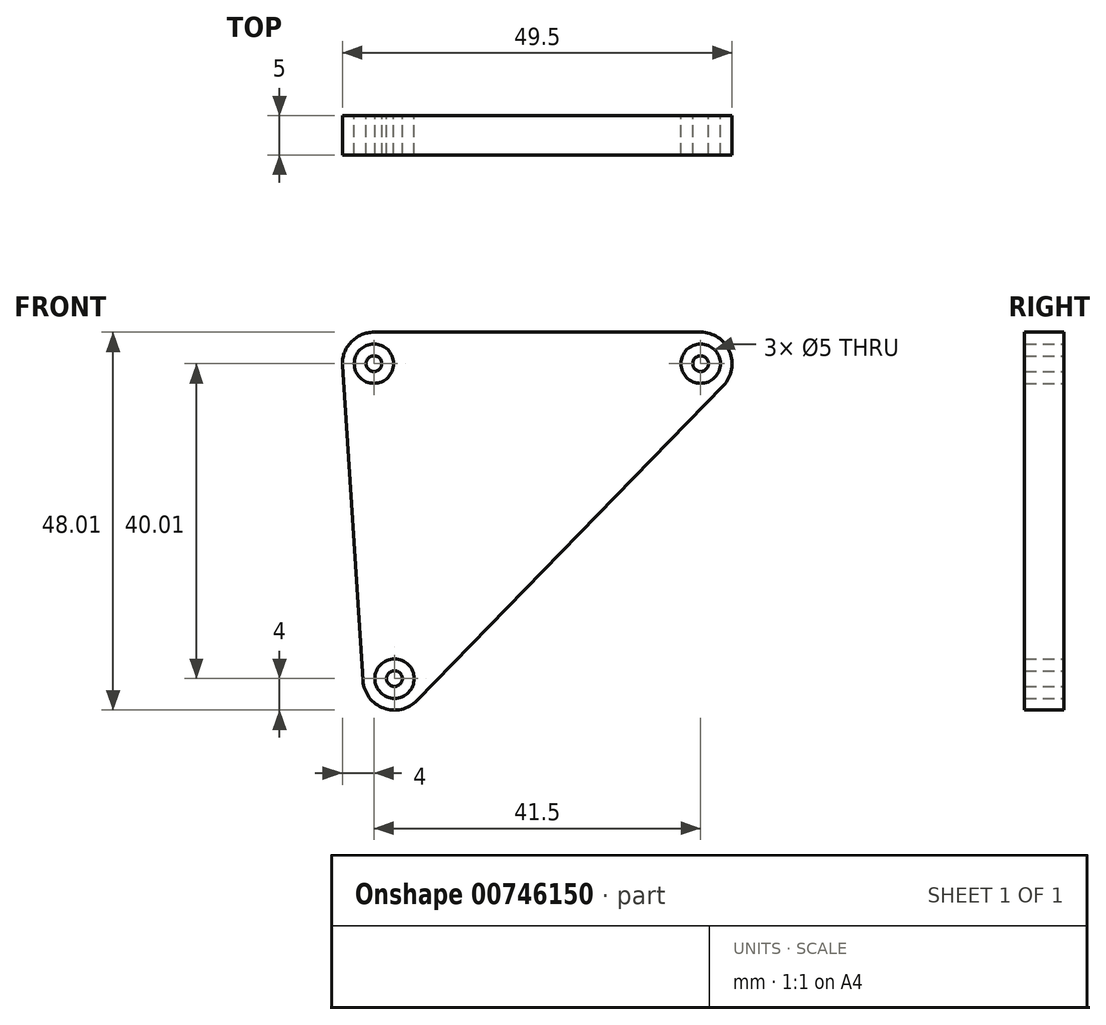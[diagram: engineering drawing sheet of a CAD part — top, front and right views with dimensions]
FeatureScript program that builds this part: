
annotation { "Feature Type Name" : "Feature", "Feature Type Description" : "" }
export const myFeature = defineFeature(function(context is Context, id is Id, definition is map)
    precondition{}
    {
        {
            var Q0;
            Q0=qCreatedBy(makeId("Front.planeOp"),FACE);
            var sketch = newSketch(context, id + "F0", { "sketchPlane" : qUnion([Q0])});
            skCircle(sketch, "E0", {"center": v(-15.71, 2.74) * mm, "radius": 2.5 * mm});
            skCircle(sketch, "E1", {"center": v(-15.71, 2.74) * mm, "radius": 1 * mm});
            skArc(sketch, "E2", {"start": v(-15.71, 6.74) * mm, "mid": v(-18.63, 5.47) * mm, "end": v(-19.7, 2.48) * mm});
            skCircle(sketch, "E3", {"center": v(25.79, 2.74) * mm, "radius": 2.5 * mm});
            skCircle(sketch, "E4", {"center": v(25.79, 2.74) * mm, "radius": 1 * mm});
            skArc(sketch, "E5", {"start": v(28.66, -0.05) * mm, "mid": v(29.47, 4.3) * mm, "end": v(25.79, 6.74) * mm});
            skArc(sketch, "E6", {"start": v(-17.1, -37.53) * mm, "mid": v(-14.48, -41.02) * mm, "end": v(-10.23, -40.06) * mm});
            skCircle(sketch, "E7", {"center": v(-13.1, -37.27) * mm, "radius": 2.5 * mm});
            skCircle(sketch, "E8", {"center": v(-13.1, -37.27) * mm, "radius": 1 * mm});
            skLineSegment(sketch, "E9", {"start": v(-19.7, 2.48) * mm, "end": v(-17.1, -37.53) * mm});
            skLineSegment(sketch, "E10", {"start": v(-15.71, 6.74) * mm, "end": v(25.79, 6.74) * mm});
            skLineSegment(sketch, "E11", {"start": v(28.66, -0.05) * mm, "end": v(-10.23, -40.06) * mm});
            skSolve(sketch);
        }
        {
            var Q0;
            Q0=makeQuery(id+"F0.imprint","IMPRINT",FACE,{"disambiguationData":[TD([[makeQuery(id+"F0.imprint","IMPRINT",EDGE,{"derivedFrom":sQuery(id+"F0.wireOp",EDGE,"E0")}),-1.0]])]});
            var Q1;
            Q1=makeQuery(id+"F0.imprint","IMPRINT",FACE,{"disambiguationData":[TD([[makeQuery(id+"F0.imprint","IMPRINT",EDGE,{"derivedFrom":sQuery(id+"F0.wireOp",EDGE,"E1")}),1.0]])]});
            var Q2;
            Q2=makeQuery(id+"F0.imprint","IMPRINT",FACE,{"disambiguationData":[TD([[makeQuery(id+"F0.imprint","IMPRINT",EDGE,{"derivedFrom":sQuery(id+"F0.wireOp",EDGE,"E4")}),1.0]])]});
            var Q3;
            Q3=makeQuery(id+"F0.imprint","IMPRINT",FACE,{"disambiguationData":[TD([[makeQuery(id+"F0.imprint","IMPRINT",EDGE,{"derivedFrom":sQuery(id+"F0.wireOp",EDGE,"E8")}),1.0]])]});
            extrude(context, id + "F1", {"entities" : qUnion([Q0, Q1, Q2, Q3]), "depth" : 5 * mm, "offsetDistance" : 25 * mm});
        }
    });
